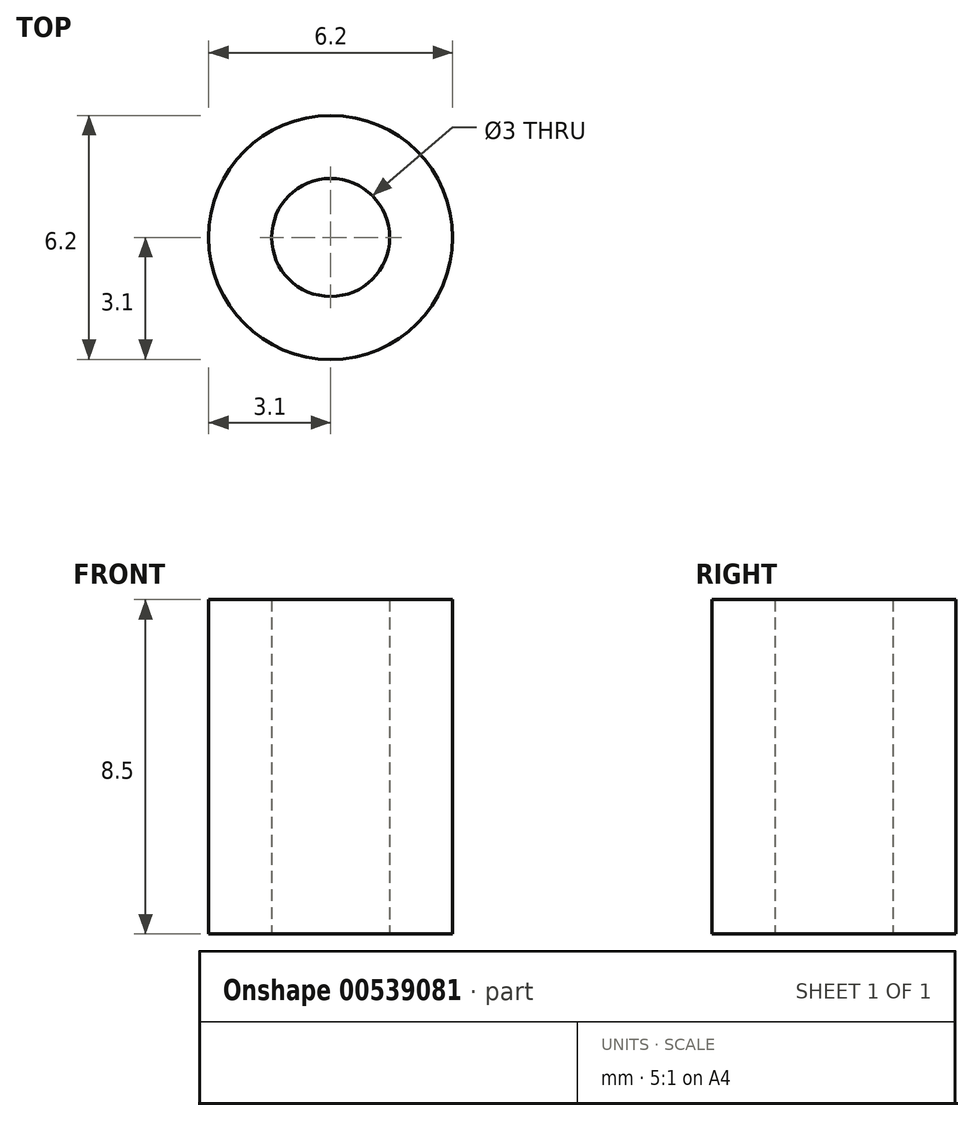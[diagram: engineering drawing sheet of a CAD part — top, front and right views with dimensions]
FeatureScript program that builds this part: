
annotation { "Feature Type Name" : "Feature", "Feature Type Description" : "" }
export const myFeature = defineFeature(function(context is Context, id is Id, definition is map)
    precondition{}
    {
        {
            var Q0;
            Q0=qCreatedBy(makeId("Top.planeOp"),FACE);
            var sketch = newSketch(context, id + "F0", { "sketchPlane" : qUnion([Q0])});
            skCircle(sketch, "E0", {"center": v(0, 0) * mm, "radius": 1.5 * mm});
            skCircle(sketch, "E1", {"center": v(0, 0) * mm, "radius": 3.1 * mm});
            skSolve(sketch);
        }
        {
            var Q0;
            Q0 = qSketchRegion(id + "F0", true);
            extrude(context, id + "F1", {"entities" : qUnion([Q0]), "depth" : 8.5 * mm, "offsetDistance" : 25 * mm});
        }
    });
